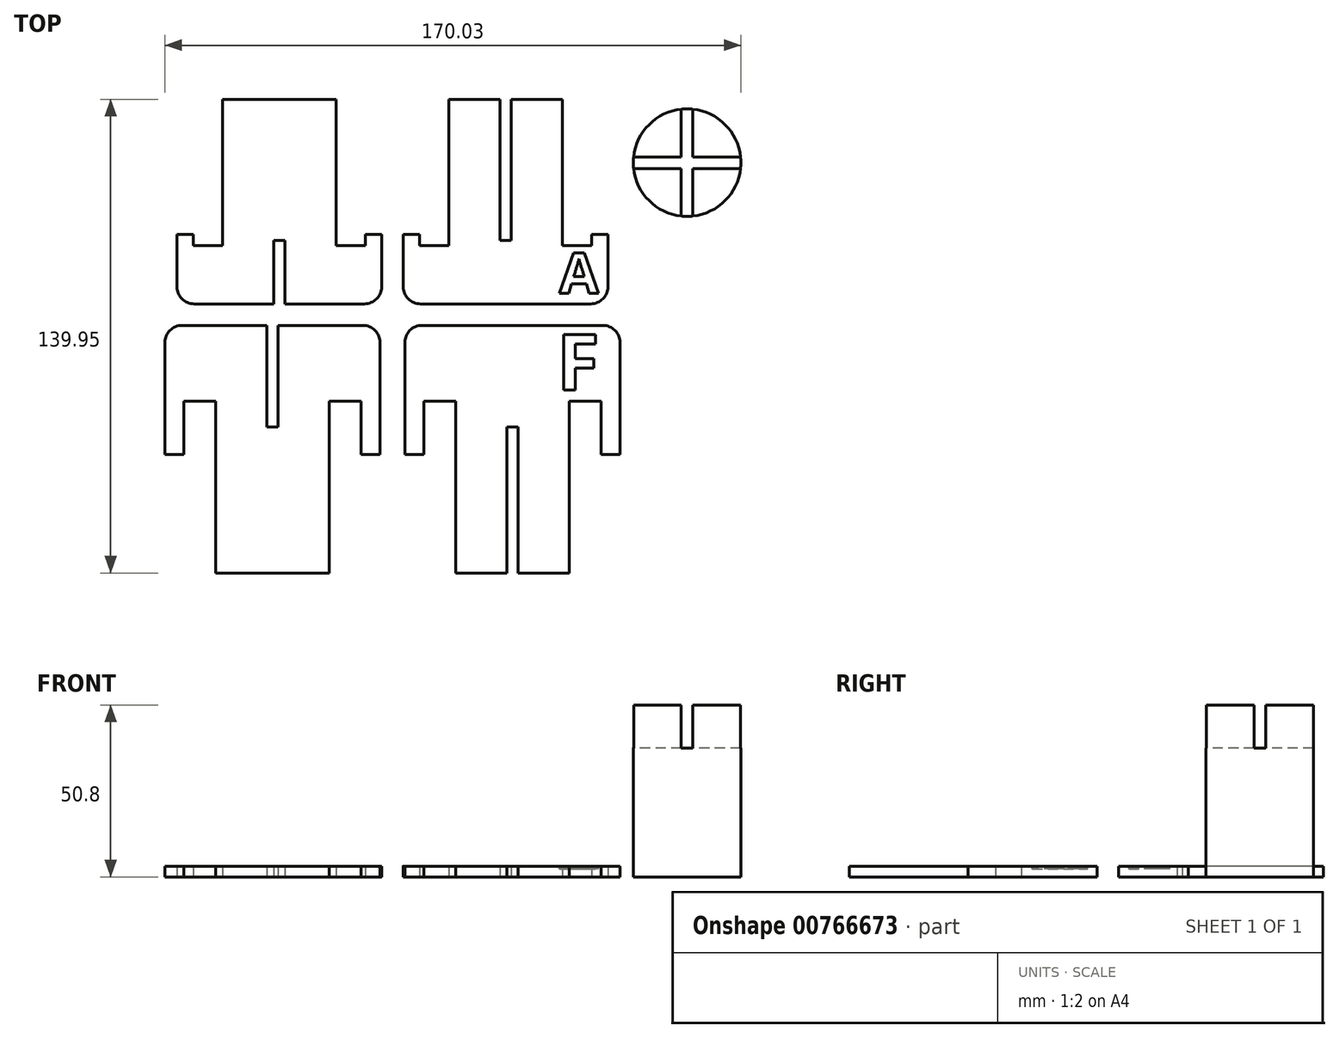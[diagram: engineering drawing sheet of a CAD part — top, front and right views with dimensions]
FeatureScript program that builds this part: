
annotation { "Feature Type Name" : "Feature", "Feature Type Description" : "" }
export const myFeature = defineFeature(function(context is Context, id is Id, definition is map)
    precondition{}
    {
        {
            var Q0;
            Q0=qCreatedBy(makeId("Top.planeOp"),FACE);
            var sketch = newSketch(context, id + "F0", { "sketchPlane" : qUnion([Q0])});
            skLineSegment(sketch, "E0.bottom", {"start": v(-37.06, 0) * mm, "end": v(-67.16, 0) * mm});
            skLineSegment(sketch, "E0.top", {"start": v(-35.41, -73.15) * mm, "end": v(-52.18, -73.15) * mm});
            skLineSegment(sketch, "E0.right", {"start": v(-67.16, 0) * mm, "end": v(-67.16, -38.1) * mm});
            skLineSegment(sketch, "E1", {"start": v(-35.41, 0) * mm, "end": v(-35.41, -73.15) * mm, "construction": true});
            skLineSegment(sketch, "E2", {"start": v(-52.18, -73.15) * mm, "end": v(-52.18, -22.35) * mm});
            skLineSegment(sketch, "E3", {"start": v(-52.18, -22.35) * mm, "end": v(-61.57, -22.35) * mm});
            skLineSegment(sketch, "E4", {"start": v(-61.57, -22.35) * mm, "end": v(-61.57, -38.1) * mm});
            skLineSegment(sketch, "E5", {"start": v(-61.57, -38.1) * mm, "end": v(-67.16, -38.1) * mm});
            skPoint(sketch, "E6.orphan", {"position": v(-67.16, -73.15) * mm});
            skPoint(sketch, "E0.left.end.orphan", {"position": v(-3.66, -73.15) * mm});
            skPoint(sketch, "E0.left.start.orphan", {"position": v(-3.66, 0) * mm});
            skLineSegment(sketch, "E7.MirrorCS", {"start": v(-33.76, 0) * mm, "end": v(-3.66, 0) * mm});
            skLineSegment(sketch, "E8.MirrorCS", {"start": v(-3.66, 0) * mm, "end": v(-3.66, -38.1) * mm});
            skLineSegment(sketch, "E9.MirrorCS", {"start": v(-9.25, -38.1) * mm, "end": v(-3.66, -38.1) * mm});
            skLineSegment(sketch, "E10.MirrorCS", {"start": v(-9.25, -22.35) * mm, "end": v(-9.25, -38.1) * mm});
            skLineSegment(sketch, "E11.MirrorCS", {"start": v(-18.65, -22.35) * mm, "end": v(-9.25, -22.35) * mm});
            skLineSegment(sketch, "E12.MirrorCS", {"start": v(-18.65, -73.15) * mm, "end": v(-18.65, -22.35) * mm});
            skLineSegment(sketch, "E13.MirrorCS", {"start": v(-35.41, -73.15) * mm, "end": v(-18.65, -73.15) * mm});
            skLineSegment(sketch, "E14.MirrorCS", {"start": v(3.66, 0) * mm, "end": v(3.66, -38.1) * mm});
            skLineSegment(sketch, "E15.MirrorCS", {"start": v(35.41, 0) * mm, "end": v(3.66, 0) * mm});
            skLineSegment(sketch, "E16.MirrorCS", {"start": v(35.41, 0) * mm, "end": v(67.16, 0) * mm});
            skLineSegment(sketch, "E17.MirrorCS", {"start": v(67.16, 0) * mm, "end": v(67.16, -38.1) * mm});
            skLineSegment(sketch, "E18.MirrorCS", {"start": v(61.57, -38.1) * mm, "end": v(67.16, -38.1) * mm});
            skLineSegment(sketch, "E19.MirrorCS", {"start": v(61.57, -22.35) * mm, "end": v(61.57, -38.1) * mm});
            skLineSegment(sketch, "E20.MirrorCS", {"start": v(52.18, -22.35) * mm, "end": v(61.57, -22.35) * mm});
            skLineSegment(sketch, "E21.MirrorCS", {"start": v(52.18, -73.15) * mm, "end": v(52.18, -22.35) * mm});
            skLineSegment(sketch, "E22.MirrorCS", {"start": v(37.06, -73.15) * mm, "end": v(52.18, -73.15) * mm});
            skLineSegment(sketch, "E23.MirrorCS", {"start": v(18.65, -73.15) * mm, "end": v(18.65, -22.35) * mm});
            skLineSegment(sketch, "E24.MirrorCS", {"start": v(33.76, -73.15) * mm, "end": v(18.65, -73.15) * mm});
            skLineSegment(sketch, "E25.MirrorCS", {"start": v(18.65, -22.35) * mm, "end": v(9.25, -22.35) * mm});
            skLineSegment(sketch, "E26.MirrorCS", {"start": v(9.25, -22.35) * mm, "end": v(9.25, -38.1) * mm});
            skLineSegment(sketch, "E27.MirrorCS", {"start": v(9.25, -38.1) * mm, "end": v(3.66, -38.1) * mm});
            skLineSegment(sketch, "E28", {"start": v(35.41, 0) * mm, "end": v(35.41, -73.15) * mm, "construction": true});
            skLineSegment(sketch, "E29", {"start": v(33.76, -73.15) * mm, "end": v(33.76, -29.97) * mm});
            skLineSegment(sketch, "E30", {"start": v(33.76, -29.97) * mm, "end": v(37.06, -29.97) * mm});
            skLineSegment(sketch, "E31", {"start": v(37.06, -29.97) * mm, "end": v(37.06, -73.15) * mm});
            skPoint(sketch, "E32.orphan", {"position": v(35.41, -73.15) * mm});
            skLineSegment(sketch, "E33", {"start": v(-33.76, -29.97) * mm, "end": v(-33.76, 0) * mm});
            skLineSegment(sketch, "E34", {"start": v(-33.76, -29.97) * mm, "end": v(-35.41, -29.97) * mm});
            skLineSegment(sketch, "E35.MirrorCS", {"start": v(-37.06, -29.97) * mm, "end": v(-37.06, 0) * mm});
            skLineSegment(sketch, "E36.MirrorCS", {"start": v(-37.06, -29.97) * mm, "end": v(-35.41, -29.97) * mm});
            skPoint(sketch, "E37.orphan", {"position": v(-35.41, 0) * mm});
            skSolve(sketch);
        }
        {
            var Q0;
            Q0 = qSketchRegion(id + "F0", true);
            extrude(context, id + "F1", {"entities" : qUnion([Q0]), "depth" : 3.17 * mm, "offsetDistance" : 25.4 * mm});
        }
        {
            var Q0;
            Q0=makeQuery(id+"F1.opExtrude","CAP_FACE",FACE,{"disambiguationData":[OSD([sQuery(id+"F0.wireOp",EDGE,"E14.MirrorCS"),sQuery(id+"F0.wireOp",EDGE,"E15.MirrorCS"),sQuery(id+"F0.wireOp",EDGE,"E16.MirrorCS"),sQuery(id+"F0.wireOp",EDGE,"E17.MirrorCS"),sQuery(id+"F0.wireOp",EDGE,"E18.MirrorCS"),sQuery(id+"F0.wireOp",EDGE,"E19.MirrorCS"),sQuery(id+"F0.wireOp",EDGE,"E20.MirrorCS"),sQuery(id+"F0.wireOp",EDGE,"E22.MirrorCS"),sQuery(id+"F0.wireOp",EDGE,"E21.MirrorCS"),sQuery(id+"F0.wireOp",EDGE,"E23.MirrorCS"),sQuery(id+"F0.wireOp",EDGE,"E24.MirrorCS"),sQuery(id+"F0.wireOp",EDGE,"E25.MirrorCS"),sQuery(id+"F0.wireOp",EDGE,"E26.MirrorCS"),sQuery(id+"F0.wireOp",EDGE,"E27.MirrorCS"),sQuery(id+"F0.wireOp",EDGE,"E29"),sQuery(id+"F0.wireOp",EDGE,"E30"),sQuery(id+"F0.wireOp",EDGE,"E31")])],"isStart":false});
            var sketch = newSketch(context, id + "F2", { "sketchPlane" : qUnion([Q0])});
            skText(sketch, "E38", { "text": "F", "fontName": "OpenSans-Bold.ttf"});
            const initialGuessF2  = {"E38": [0.04844, -0.01912, 1, 0, 0.01654]};
            skSetInitialGuess(sketch, initialGuessF2);
            skSolve(sketch);
        }
        {
            var Q0;
            Q0 = qSketchRegion(id + "F2", true);
            extrude(context, id + "F3", {"entities" : qUnion([Q0]), "operationType" : NewBodyOperationType.REMOVE, "oppositeDirection" : true, "depth" : 0.76 * mm, "offsetDistance" : 25.4 * mm});
        }
        {
            var Q0;
            Q0=qCreatedBy(makeId("Top.planeOp"),FACE);
            var sketch = newSketch(context, id + "F4", { "sketchPlane" : qUnion([Q0])});
            skLineSegment(sketch, "E39.bottom", {"start": v(-3.17, 6.35) * mm, "end": v(-31.75, 6.35) * mm});
            skLineSegment(sketch, "E39.top", {"start": v(-33.4, 66.8) * mm, "end": v(-50.16, 66.8) * mm});
            skLineSegment(sketch, "E39.right", {"start": v(-63.63, 6.35) * mm, "end": v(-63.63, 26.92) * mm});
            skLineSegment(sketch, "E40", {"start": v(-33.4, 66.8) * mm, "end": v(-33.4, 6.35) * mm, "construction": true});
            skLineSegment(sketch, "E41", {"start": v(-50.17, 66.8) * mm, "end": v(-50.16, 23.62) * mm});
            skLineSegment(sketch, "E42", {"start": v(-50.16, 23.62) * mm, "end": v(-58.8, 23.62) * mm});
            skLineSegment(sketch, "E43", {"start": v(-58.8, 23.62) * mm, "end": v(-58.8, 26.92) * mm});
            skLineSegment(sketch, "E44", {"start": v(-58.8, 26.92) * mm, "end": v(-63.63, 26.92) * mm});
            skPoint(sketch, "E45.orphan", {"position": v(-63.63, 66.8) * mm});
            skPoint(sketch, "E39.left.end.orphan", {"position": v(-3.18, 66.8) * mm});
            skLineSegment(sketch, "E46.MirrorCS", {"start": v(-33.4, 66.8) * mm, "end": v(-16.64, 66.8) * mm});
            skLineSegment(sketch, "E47.MirrorCS", {"start": v(-16.64, 66.8) * mm, "end": v(-16.64, 23.62) * mm});
            skLineSegment(sketch, "E48.MirrorCS", {"start": v(-16.64, 23.62) * mm, "end": v(-8, 23.62) * mm});
            skLineSegment(sketch, "E49.MirrorCS", {"start": v(-8, 23.62) * mm, "end": v(-8, 26.92) * mm});
            skLineSegment(sketch, "E50.MirrorCS", {"start": v(-8, 26.92) * mm, "end": v(-3.17, 26.92) * mm});
            skLineSegment(sketch, "E51.MirrorCS", {"start": v(-3.17, 6.35) * mm, "end": v(-3.17, 26.92) * mm});
            skLineSegment(sketch, "E52.MirrorCS", {"start": v(3.18, 6.35) * mm, "end": v(3.18, 26.92) * mm});
            skLineSegment(sketch, "E53.MirrorCS", {"start": v(8, 26.92) * mm, "end": v(3.17, 26.92) * mm});
            skLineSegment(sketch, "E54.MirrorCS", {"start": v(16.64, 23.62) * mm, "end": v(8, 23.62) * mm});
            skLineSegment(sketch, "E55.MirrorCS", {"start": v(3.17, 6.35) * mm, "end": v(63.63, 6.35) * mm});
            skLineSegment(sketch, "E56.MirrorCS", {"start": v(63.63, 6.35) * mm, "end": v(63.63, 26.92) * mm});
            skLineSegment(sketch, "E57.MirrorCS", {"start": v(58.8, 26.92) * mm, "end": v(63.63, 26.92) * mm});
            skLineSegment(sketch, "E58.MirrorCS", {"start": v(58.8, 23.62) * mm, "end": v(58.8, 26.92) * mm});
            skLineSegment(sketch, "E59.MirrorCS", {"start": v(50.16, 23.62) * mm, "end": v(58.8, 23.62) * mm});
            skLineSegment(sketch, "E60.MirrorCS", {"start": v(50.16, 66.8) * mm, "end": v(50.16, 23.62) * mm});
            skLineSegment(sketch, "E61.MirrorCS", {"start": v(35.05, 66.8) * mm, "end": v(50.16, 66.8) * mm});
            skLineSegment(sketch, "E62.MirrorCS", {"start": v(31.75, 66.8) * mm, "end": v(16.64, 66.8) * mm});
            skLineSegment(sketch, "E63.MirrorCS", {"start": v(16.64, 66.8) * mm, "end": v(16.64, 23.62) * mm});
            skLineSegment(sketch, "E64.MirrorCS", {"start": v(8, 23.62) * mm, "end": v(8, 26.92) * mm});
            skLineSegment(sketch, "E65", {"start": v(33.4, 66.8) * mm, "end": v(33.4, 6.35) * mm, "construction": true});
            skLineSegment(sketch, "E66", {"start": v(-31.75, 6.35) * mm, "end": v(-31.75, 25.15) * mm});
            skLineSegment(sketch, "E67", {"start": v(-31.75, 25.15) * mm, "end": v(-33.4, 25.15) * mm});
            skLineSegment(sketch, "E68", {"start": v(31.75, 66.8) * mm, "end": v(31.75, 25.15) * mm});
            skLineSegment(sketch, "E69", {"start": v(31.75, 25.15) * mm, "end": v(33.4, 25.15) * mm});
            skLineSegment(sketch, "E70.MirrorCS", {"start": v(-35.05, 6.35) * mm, "end": v(-35.05, 25.15) * mm});
            skLineSegment(sketch, "E71.MirrorCS", {"start": v(-35.05, 25.15) * mm, "end": v(-33.4, 25.15) * mm});
            skLineSegment(sketch, "E72.MirrorCS", {"start": v(35.05, 66.8) * mm, "end": v(35.05, 25.15) * mm});
            skLineSegment(sketch, "E73.MirrorCS", {"start": v(35.05, 25.15) * mm, "end": v(33.4, 25.15) * mm});
            skLineSegment(sketch, "E74", {"start": v(31.75, 25.15) * mm, "end": v(-31.75, 25.15) * mm, "construction": true});
            skPoint(sketch, "E75.orphan", {"position": v(33.4, 66.8) * mm});
            skLineSegment(sketch, "E76.trimOffspring", {"start": v(-35.05, 6.35) * mm, "end": v(-63.63, 6.35) * mm});
            skSolve(sketch);
        }
        {
            var Q0;
            Q0 = qSketchRegion(id + "F4", true);
            extrude(context, id + "F5", {"entities" : qUnion([Q0]), "depth" : 3.17 * mm, "offsetDistance" : 25.4 * mm});
        }
        {
            var Q0;
            Q0=makeQuery(id+"F5.opExtrude","CAP_FACE",FACE,{"disambiguationData":[OSD([sQuery(id+"F4.wireOp",EDGE,"E52.MirrorCS"),sQuery(id+"F4.wireOp",EDGE,"E53.MirrorCS"),sQuery(id+"F4.wireOp",EDGE,"E55.MirrorCS"),sQuery(id+"F4.wireOp",EDGE,"E56.MirrorCS"),sQuery(id+"F4.wireOp",EDGE,"E57.MirrorCS"),sQuery(id+"F4.wireOp",EDGE,"E58.MirrorCS"),sQuery(id+"F4.wireOp",EDGE,"E59.MirrorCS"),sQuery(id+"F4.wireOp",EDGE,"E60.MirrorCS"),sQuery(id+"F4.wireOp",EDGE,"E61.MirrorCS"),sQuery(id+"F4.wireOp",EDGE,"E62.MirrorCS"),sQuery(id+"F4.wireOp",EDGE,"E63.MirrorCS"),sQuery(id+"F4.wireOp",EDGE,"E54.MirrorCS"),sQuery(id+"F4.wireOp",EDGE,"E64.MirrorCS")])],"isStart":false});
            var sketch = newSketch(context, id + "F6", { "sketchPlane" : qUnion([Q0])});
            skText(sketch, "E77", { "text": "A", "fontName": "OpenSans-Bold.ttf"});
            const initialGuessF6  = {"E77": [0.0493, 0.00945, 1, 0, 0.01203]};
            skSetInitialGuess(sketch, initialGuessF6);
            skSolve(sketch);
        }
        {
            var Q0;
            Q0 = qSketchRegion(id + "F6", true);
            extrude(context, id + "F7", {"entities" : qUnion([Q0]), "operationType" : NewBodyOperationType.REMOVE, "oppositeDirection" : true, "depth" : 0.76 * mm, "offsetDistance" : 25.4 * mm});
        }
        {
            var Q0;
            Q0=makeQuery(id+"F5.opExtrude","SWEPT_EDGE",EDGE,{"disambiguationData":[OSD([sQuery(id+"F4.wireOp",EDGE,"E52.MirrorCS"),sQuery(id+"F4.wireOp",EDGE,"E55.MirrorCS")])]});
            var Q1;
            Q1=makeQuery(id+"F5.opExtrude","SWEPT_EDGE",EDGE,{"disambiguationData":[OSD([sQuery(id+"F4.wireOp",EDGE,"E55.MirrorCS"),sQuery(id+"F4.wireOp",EDGE,"E56.MirrorCS")])]});
            var Q2;
            Q2=makeQuery(id+"F1.opExtrude","SWEPT_EDGE",EDGE,{"disambiguationData":[OSD([sQuery(id+"F0.wireOp",EDGE,"E16.MirrorCS"),sQuery(id+"F0.wireOp",EDGE,"E17.MirrorCS")])]});
            var Q3;
            Q3=makeQuery(id+"F1.opExtrude","SWEPT_EDGE",EDGE,{"disambiguationData":[OSD([sQuery(id+"F0.wireOp",EDGE,"E14.MirrorCS"),sQuery(id+"F0.wireOp",EDGE,"E15.MirrorCS")])]});
            var Q4;
            Q4=makeQuery(id+"F1.opExtrude","SWEPT_EDGE",EDGE,{"disambiguationData":[OSD([sQuery(id+"F0.wireOp",EDGE,"E7.MirrorCS"),sQuery(id+"F0.wireOp",EDGE,"E8.MirrorCS")])]});
            var Q5;
            Q5=makeQuery(id+"F1.opExtrude","SWEPT_EDGE",EDGE,{"disambiguationData":[OSD([sQuery(id+"F0.wireOp",EDGE,"E0.bottom"),sQuery(id+"F0.wireOp",EDGE,"E0.right")])]});
            var Q6;
            Q6=makeQuery(id+"F5.opExtrude","SWEPT_EDGE",EDGE,{"disambiguationData":[OSD([sQuery(id+"F4.wireOp",EDGE,"E39.right"),sQuery(id+"F4.wireOp",EDGE,"E76.trimOffspring")])]});
            var Q7;
            Q7=makeQuery(id+"F5.opExtrude","SWEPT_EDGE",EDGE,{"disambiguationData":[OSD([sQuery(id+"F4.wireOp",EDGE,"E39.bottom"),sQuery(id+"F4.wireOp",EDGE,"E51.MirrorCS")])]});
            fillet(context, id + "F8", {"entities" : qUnion([Q0, Q1, Q2, Q3, Q4, Q5, Q6, Q7]), "radius" : 5.08 * mm, "tangentPropagation" : true, "allowEdgeOverflow" : false});
        }
        {
            var Q0;
            Q0=qCreatedBy(makeId("Top.planeOp"),FACE);
            var sketch = newSketch(context, id + "F9", { "sketchPlane" : qUnion([Q0])});
            skCircle(sketch, "E78", {"center": v(87, 48.07) * mm, "radius": 15.88 * mm});
            skSolve(sketch);
        }
        {
            var Q0;
            Q0 = qSketchRegion(id + "F9", true);
            extrude(context, id + "F10", {"entities" : qUnion([Q0]), "depth" : 50.8 * mm, "offsetDistance" : 25.4 * mm});
        }
        {
            var Q0;
            Q0=makeQuery(id+"F10.opExtrude","CAP_FACE",FACE,{"disambiguationData":[OSD([sQuery(id+"F9.wireOp",EDGE,"E78")])],"isStart":false});
            var sketch = newSketch(context, id + "F11", { "sketchPlane" : qUnion([Q0])});
            skLineSegment(sketch, "E79.bottom", {"start": v(85.28, 63.95) * mm, "end": v(88.7, 63.95) * mm});
            skLineSegment(sketch, "E79.top", {"start": v(85.28, 32.2) * mm, "end": v(88.7, 32.2) * mm});
            skLineSegment(sketch, "E79.left", {"start": v(85.28, 63.95) * mm, "end": v(85.28, 32.2) * mm});
            skLineSegment(sketch, "E79.right", {"start": v(88.7, 63.95) * mm, "end": v(88.7, 32.2) * mm});
            skPoint(sketch, "E79.middle", {"position": v(87, 48.07) * mm});
            skLineSegment(sketch, "E80.bottom", {"start": v(102.87, 46.36) * mm, "end": v(71.12, 46.36) * mm});
            skLineSegment(sketch, "E80.top", {"start": v(102.87, 49.79) * mm, "end": v(71.12, 49.79) * mm});
            skLineSegment(sketch, "E80.left", {"start": v(102.87, 46.36) * mm, "end": v(102.87, 49.79) * mm});
            skLineSegment(sketch, "E80.right", {"start": v(71.12, 46.36) * mm, "end": v(71.12, 49.79) * mm});
            skSolve(sketch);
        }
        {
            var Q0;
            Q0 = qSketchRegion(id + "F11", true);
            extrude(context, id + "F12", {"entities" : qUnion([Q0]), "operationType" : NewBodyOperationType.REMOVE, "oppositeDirection" : true, "depth" : 12.7 * mm, "offsetDistance" : 25.4 * mm});
        }
    });
